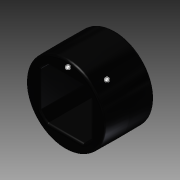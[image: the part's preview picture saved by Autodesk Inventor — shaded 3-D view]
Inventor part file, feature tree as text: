
AUTODESK INVENTOR PART (.ipt)
format: ipt  version: 2015 (Build 190159000, 159)  size: 231,936 bytes
history: native  units: in
note: dims shown in document units (in); Inventor stores cm internally (conversion verified against a paired STEP export)
features: fillet x1, other x1, imported_body x1
ambient origin geometry x8: Origin, YZ Plane, XZ Plane, XY Plane, X Axis, Y Axis, Z Axis, Center Point
bodies: Body1 (feature_tree)
feature tree (3):
  fillet  "Fillet1"  [1 undecoded]
  other  "Spacer HS 0.5 unit"
  imported_body  "Base1"
note: 1 required parameter value undecoded (feature->parameter linkage not recoverable at this tier; creation-order binding heuristic only, values carry confidence <= 0.55)
